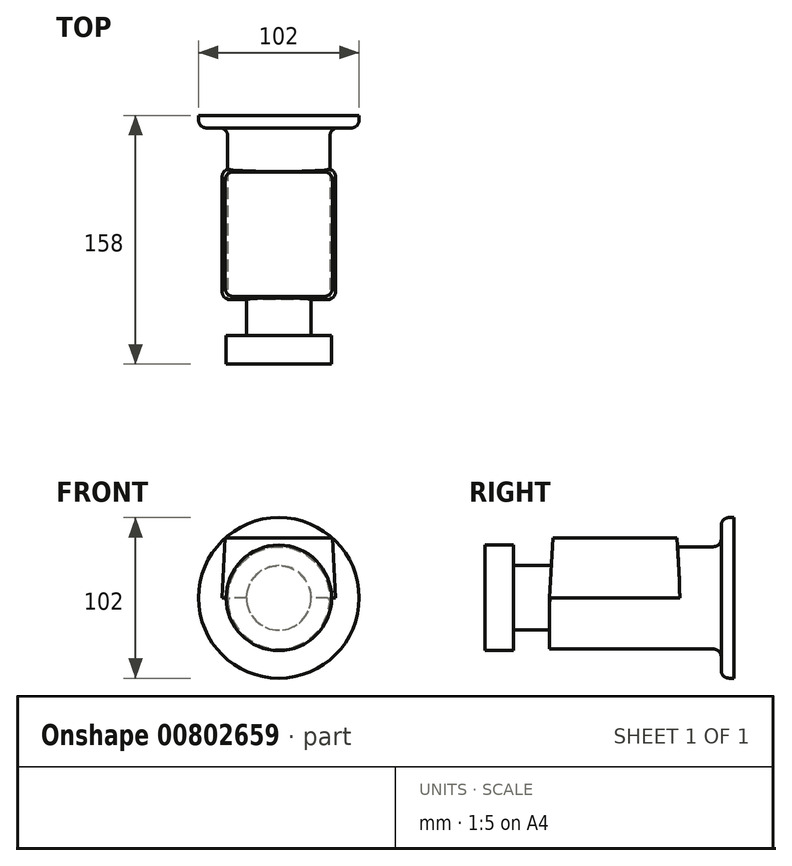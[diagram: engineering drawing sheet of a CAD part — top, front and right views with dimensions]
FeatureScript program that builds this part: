
annotation { "Feature Type Name" : "Feature", "Feature Type Description" : "" }
export const myFeature = defineFeature(function(context is Context, id is Id, definition is map)
    precondition{}
    {
        {
            var Q0;
            Q0=qCreatedBy(makeId("Front.planeOp"),FACE);
            var sketch = newSketch(context, id + "F0", { "sketchPlane" : qUnion([Q0])});
            skCircle(sketch, "E0", {"center": v(0, 0) * mm, "radius": 33.5 * mm});
            skSolve(sketch);
        }
        {
            var Q0;
            Q0 = qSketchRegion(id + "F0", true);
            extrude(context, id + "F1", {"entities" : qUnion([Q0]), "oppositeDirection" : true, "depth" : 18 * mm, "offsetDistance" : 25 * mm});
        }
        {
            var Q0;
            Q0=makeQuery(id+"F1.opExtrude","CAP_FACE",FACE,{"disambiguationData":[OSD([sQuery(id+"F0.wireOp",EDGE,"E0")])],"isStart":false});
            var sketch = newSketch(context, id + "F2", { "sketchPlane" : qUnion([Q0])});
            skCircle(sketch, "E1", {"center": v(0, 0) * mm, "radius": 20.5 * mm});
            skSolve(sketch);
        }
        {
            var Q0;
            Q0 = qSketchRegion(id + "F2", true);
            extrude(context, id + "F3", {"entities" : qUnion([Q0]), "operationType" : NewBodyOperationType.ADD, "depth" : 23 * mm, "offsetDistance" : 25 * mm});
        }
        {
            var Q0;
            Q0=makeQuery(id+"F3.opExtrude","CAP_FACE",FACE,{"disambiguationData":[OSD([sQuery(id+"F2.wireOp",EDGE,"E1")])],"isStart":false});
            var sketch = newSketch(context, id + "F4", { "sketchPlane" : qUnion([Q0])});
            skCircle(sketch, "E2", {"center": v(0, 0) * mm, "radius": 32.5 * mm});
            skSolve(sketch);
        }
        {
            var Q0;
            Q0 = qSketchRegion(id + "F4", true);
            extrude(context, id + "F5", {"entities" : qUnion([Q0]), "operationType" : NewBodyOperationType.ADD, "depth" : 117 * mm, "offsetDistance" : 25 * mm});
        }
        {
            var Q0;
            Q0=makeQuery(id+"F5.opExtrude","CAP_FACE",FACE,{"disambiguationData":[OSD([sQuery(id+"F4.wireOp",EDGE,"E2")])],"isStart":false});
            var sketch = newSketch(context, id + "F6", { "sketchPlane" : qUnion([Q0])});
            skCircle(sketch, "E3", {"center": v(0, 0) * mm, "radius": 51 * mm});
            skSolve(sketch);
        }
        {
            var Q0;
            Q0 = qSketchRegion(id + "F6", true);
            extrude(context, id + "F7", {"entities" : qUnion([Q0]), "operationType" : NewBodyOperationType.ADD, "oppositeDirection" : true, "depth" : 8 * mm, "offsetDistance" : 25 * mm});
        }
        {
            var Q0;
            Q0=qCreatedBy(makeId("Top.planeOp"),FACE);
            var sketch = newSketch(context, id + "F8", { "sketchPlane" : qUnion([Q0])});
            skLineSegment(sketch, "E4", {"start": v(0, 0) * mm, "end": v(0, 41) * mm});
            skLineSegment(sketch, "E5", {"start": v(0, 41) * mm, "end": v(36, 41) * mm});
            skLineSegment(sketch, "E6", {"start": v(36, 41) * mm, "end": v(36, 124) * mm});
            skLineSegment(sketch, "E7", {"start": v(36, 124) * mm, "end": v(-36, 124) * mm});
            skLineSegment(sketch, "E8", {"start": v(-36, 124) * mm, "end": v(-36, 41) * mm});
            skLineSegment(sketch, "E9", {"start": v(-36, 41) * mm, "end": v(0, 41) * mm});
            skSolve(sketch);
        }
        {
            var Q0;
            Q0 = qSketchRegion(id + "F8", true);
            extrude(context, id + "F9", {"entities" : qUnion([Q0]), "operationType" : NewBodyOperationType.ADD, "depth" : 38 * mm, "offsetDistance" : 25 * mm});
        }
        {
            var Q0;
            Q0=makeQuery(id+"F9.boolean.opBoolean","MERGE",FACE,{"derivedFrom":[makeQuery(id+"F5.opExtrude","CAP_FACE",FACE,{"disambiguationData":[OSD([sQuery(id+"F4.wireOp",EDGE,"E2")])],"isStart":true}),makeQuery(id+"F9.opExtrude","SWEPT_FACE",FACE,{"disambiguationData":[OSD([sQuery(id+"F8.wireOp",EDGE,"E5"),sQuery(id+"F8.wireOp",EDGE,"E9")])]})]});
            var sketch = newSketch(context, id + "F10", { "sketchPlane" : qUnion([Q0])});
            skLineSegment(sketch, "E10", {"start": v(-36, 0) * mm, "end": v(-36, 38) * mm});
            skLineSegment(sketch, "E11", {"start": v(-36, 38) * mm, "end": v(-34, 38) * mm});
            skLineSegment(sketch, "E12", {"start": v(-34, 38) * mm, "end": v(-36, 0) * mm});
            skLineSegment(sketch, "E13", {"start": v(36, 0) * mm, "end": v(36, 38) * mm});
            skLineSegment(sketch, "E14", {"start": v(36, 38) * mm, "end": v(34, 38) * mm});
            skLineSegment(sketch, "E15", {"start": v(34, 38) * mm, "end": v(36, 0) * mm});
            skSolve(sketch);
        }
        {
            var Q0;
            Q0 = qSketchRegion(id + "F10", true);
            extrude(context, id + "F11", {"entities" : qUnion([Q0]), "operationType" : NewBodyOperationType.REMOVE, "oppositeDirection" : true, "depth" : 85 * mm, "offsetDistance" : 25 * mm});
        }
        {
            var Q0;
            Q0=qCreatedBy(makeId("Right.planeOp"),FACE);
            var sketch = newSketch(context, id + "F12", { "sketchPlane" : qUnion([Q0])});
            skLineSegment(sketch, "E16", {"start": v(124, 0) * mm, "end": v(124, 38) * mm});
            skLineSegment(sketch, "E17", {"start": v(124, 38) * mm, "end": v(122, 38) * mm});
            skLineSegment(sketch, "E18", {"start": v(122, 38) * mm, "end": v(124, 0) * mm});
            skLineSegment(sketch, "E19", {"start": v(41, 0) * mm, "end": v(41, 38) * mm});
            skLineSegment(sketch, "E20", {"start": v(41, 38) * mm, "end": v(43, 38) * mm});
            skLineSegment(sketch, "E21", {"start": v(43, 38) * mm, "end": v(41, 0) * mm});
            skSolve(sketch);
        }
        {
            var Q0;
            Q0 = qSketchRegion(id + "F12", true);
            extrude(context, id + "F13", {"entities" : qUnion([Q0]), "operationType" : NewBodyOperationType.REMOVE, "endBound" : BoundingType.SYMMETRIC, "depth" : 72 * mm, "offsetDistance" : 25 * mm});
        }
        {
            var Q0;
            Q0 = qSketchRegion(id + "F2", true);
            extrude(context, id + "F14", {"entities" : qUnion([Q0]), "operationType" : NewBodyOperationType.ADD, "depth" : 30 * mm, "offsetDistance" : 25 * mm});
        }
        {
            var Q0;
            Q0=makeQuery(id+"F7.boolean.opBoolean","MERGE",FACE,{"derivedFrom":[makeQuery(id+"F5.opExtrude","CAP_FACE",FACE,{"disambiguationData":[OSD([sQuery(id+"F4.wireOp",EDGE,"E2")])],"isStart":false}),makeQuery(id+"F7.opExtrude","CAP_FACE",FACE,{"disambiguationData":[OSD([sQuery(id+"F6.wireOp",EDGE,"E3")])],"isStart":true})]});
            var sketch = newSketch(context, id + "F15", { "sketchPlane" : qUnion([Q0])});
            skCircle(sketch, "E22", {"center": v(0, 0) * mm, "radius": 32.5 * mm});
            skSolve(sketch);
        }
        {
            var Q0;
            Q0 = qSketchRegion(id + "F15", true);
            extrude(context, id + "F16", {"entities" : qUnion([Q0]), "operationType" : NewBodyOperationType.ADD, "oppositeDirection" : true, "depth" : 50 * mm, "offsetDistance" : 25 * mm});
        }
        {
            var Q0;
            Q0=makeQuery(id+"F13.boolean.opBoolean","INTERSECT",EDGE,{"derivedFrom":[makeQuery(id+"F11.boolean.opBoolean","COPY",FACE,{"derivedFrom":makeQuery(id+"F11.opExtrude","SWEPT_FACE",FACE,{"disambiguationData":[OSD([sQuery(id+"F10.wireOp",EDGE,"E12")])]})}),makeQuery(id+"F13.opExtrude","SWEPT_FACE",FACE,{"disambiguationData":[OSD([sQuery(id+"F12.wireOp",EDGE,"E18")])]})]});
            var Q1;
            Q1=makeQuery(id+"F13.boolean.opBoolean","INTERSECT",EDGE,{"derivedFrom":[makeQuery(id+"F11.boolean.opBoolean","COPY",FACE,{"derivedFrom":makeQuery(id+"F11.opExtrude","SWEPT_FACE",FACE,{"disambiguationData":[OSD([sQuery(id+"F10.wireOp",EDGE,"E12")])]})}),makeQuery(id+"F13.opExtrude","SWEPT_FACE",FACE,{"disambiguationData":[OSD([sQuery(id+"F12.wireOp",EDGE,"E21")])]})]});
            var Q2;
            Q2=makeQuery(id+"F13.boolean.opBoolean","INTERSECT",EDGE,{"derivedFrom":[makeQuery(id+"F11.boolean.opBoolean","COPY",FACE,{"derivedFrom":makeQuery(id+"F11.opExtrude","SWEPT_FACE",FACE,{"disambiguationData":[OSD([sQuery(id+"F10.wireOp",EDGE,"E15")])]})}),makeQuery(id+"F13.opExtrude","SWEPT_FACE",FACE,{"disambiguationData":[OSD([sQuery(id+"F12.wireOp",EDGE,"E21")])]})]});
            var Q3;
            Q3=makeQuery(id+"F13.boolean.opBoolean","INTERSECT",EDGE,{"derivedFrom":[makeQuery(id+"F11.boolean.opBoolean","COPY",FACE,{"derivedFrom":makeQuery(id+"F11.opExtrude","SWEPT_FACE",FACE,{"disambiguationData":[OSD([sQuery(id+"F10.wireOp",EDGE,"E15")])]})}),makeQuery(id+"F13.opExtrude","SWEPT_FACE",FACE,{"disambiguationData":[OSD([sQuery(id+"F12.wireOp",EDGE,"E18")])]})]});
            fillet(context, id + "F17", {"entities" : qUnion([Q0, Q1, Q2, Q3]), "radius" : 5 * mm, "tangentPropagation" : true, "allowEdgeOverflow" : false});
        }
        {
            var Q0;
            Q0=makeQuery(id+"F7.opExtrude","CAP_EDGE",EDGE,{"disambiguationData":[OSD([sQuery(id+"F6.wireOp",EDGE,"E3")])],"isStart":false});
            var Q1;
            Q1=makeQuery(id+"F7.boolean.opBoolean","INTERSECT",EDGE,{"derivedFrom":[makeQuery(id+"F5.opExtrude","SWEPT_FACE",FACE,{"disambiguationData":[OSD([sQuery(id+"F4.wireOp",EDGE,"E2")])]}),makeQuery(id+"F7.opExtrude","CAP_FACE",FACE,{"disambiguationData":[OSD([sQuery(id+"F6.wireOp",EDGE,"E3")])],"isStart":false})]});
            fillet(context, id + "F18", {"entities" : qUnion([Q0, Q1]), "radius" : 5 * mm, "tangentPropagation" : true, "allowEdgeOverflow" : false});
        }
    });
